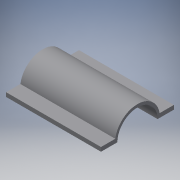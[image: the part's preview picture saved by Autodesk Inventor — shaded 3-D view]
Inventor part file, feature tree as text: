
AUTODESK INVENTOR PART (.ipt)
format: ipt  version: 2016 SP1 (Build 200210100, 210)  size: 117,248 bytes
history: native  units: in
note: dims shown in document units (in); Inventor stores cm internally (conversion verified against a paired STEP export)
features: extrude x1
ambient origin geometry x8: Origin, YZ Plane, XZ Plane, XY Plane, X Axis, Y Axis, Z Axis, Center Point
bodies: Solid1 (feature_tree)
feature tree (1):
  extrude  "Extrusion1"  Depth=0.9843in
